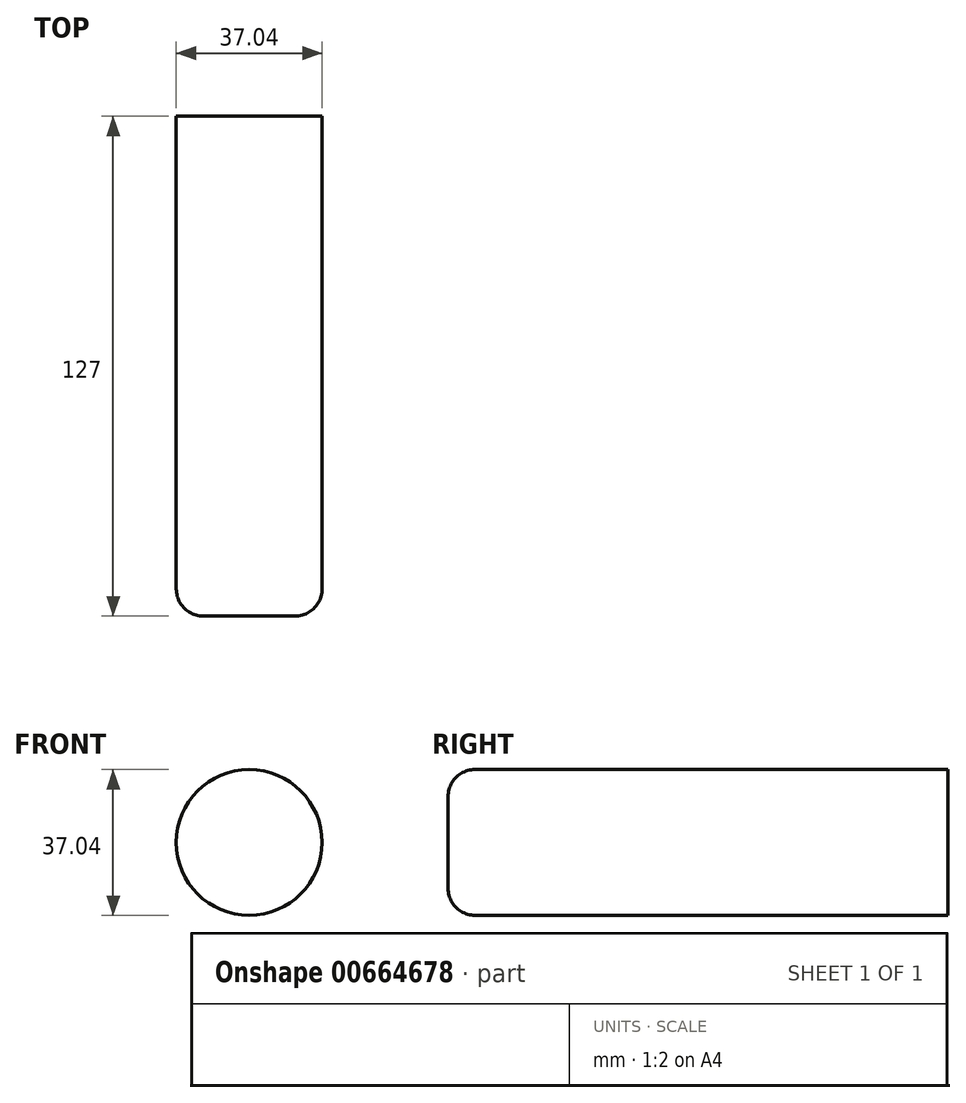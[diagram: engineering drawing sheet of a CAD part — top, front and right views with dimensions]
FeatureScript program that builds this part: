
annotation { "Feature Type Name" : "Feature", "Feature Type Description" : "" }
export const myFeature = defineFeature(function(context is Context, id is Id, definition is map)
    precondition{}
    {
        {
            var Q0;
            Q0=qCreatedBy(makeId("Front.planeOp"),FACE);
            var sketch = newSketch(context, id + "F0", { "sketchPlane" : qUnion([Q0])});
            skPoint(sketch, "E0.0", {"position": v(0, 0) * mm});
            skCircle(sketch, "E1", {"center": v(0, 0) * mm, "radius": 18.52 * mm});
            skSolve(sketch);
        }
        {
            var Q0;
            Q0 = qSketchRegion(id + "F0", true);
            extrude(context, id + "F1", {"entities" : qUnion([Q0]), "depth" : 127 * mm, "offsetDistance" : 25.4 * mm});
        }
        {
            var Q0;
            Q0=makeQuery(id+"F1.opExtrude","CAP_EDGE",EDGE,{"disambiguationData":[OSD([sQuery(id+"F0.wireOp",EDGE,"E1")])],"isStart":false});
            fillet(context, id + "F2", {"entities" : qUnion([Q0]), "radius" : 6.87 * mm, "tangentPropagation" : true, "allowEdgeOverflow" : false});
        }
    });
